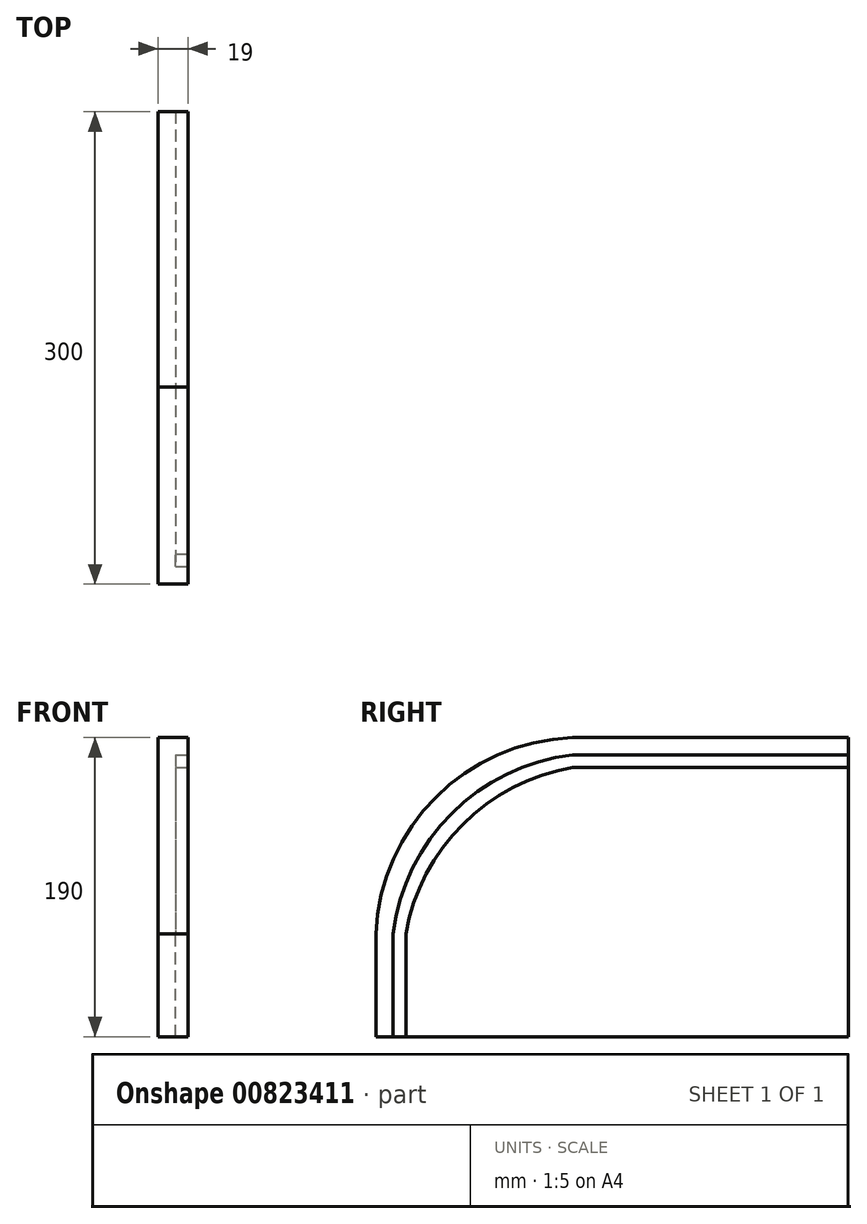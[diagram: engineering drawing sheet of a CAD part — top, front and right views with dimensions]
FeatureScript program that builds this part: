
annotation { "Feature Type Name" : "Feature", "Feature Type Description" : "" }
export const myFeature = defineFeature(function(context is Context, id is Id, definition is map)
    precondition{}
    {
        {
            var Q0;
            Q0=qCreatedBy(makeId("Right.planeOp"),FACE);
            var sketch = newSketch(context, id + "F0", { "sketchPlane" : qUnion([Q0])});
            skLineSegment(sketch, "E0.bottom", {"start": v(-25, 95) * mm, "end": v(150, 95) * mm});
            skLineSegment(sketch, "E0.top", {"start": v(-150, -95) * mm, "end": v(150, -95) * mm});
            skLineSegment(sketch, "E0.left", {"start": v(-150, -29.82) * mm, "end": v(-150, -95) * mm});
            skLineSegment(sketch, "E0.right", {"start": v(150, 95) * mm, "end": v(150, -95) * mm});
            skPoint(sketch, "E0.middle", {"position": v(0, 0) * mm});
            skPoint(sketch, "E1", {"position": v(-150, -40) * mm});
            skPoint(sketch, "E2", {"position": v(-25, 95) * mm});
            skArc(sketch, "E3", {"start": v(-25, 95) * mm, "mid": v(-115.49, 53.42) * mm, "end": v(-150, -40) * mm});
            skPoint(sketch, "E4.orphan", {"position": v(-150, 95) * mm});
            skSolve(sketch);
        }
        {
            var Q0;
            {var subQ5=sQuery(id+"F0.wireOp",EDGE,"E0.bottom");Q0=makeQuery(id+"F0.imprint","IMPRINT",FACE,{"disambiguationData":[TD([[makeQuery(id+"F0.imprint","IMPRINT",EDGE,{"derivedFrom":subQ5}),-1.0]])]});}
            extrude(context, id + "F1", {"entities" : qUnion([Q0]), "depth" : 19 * mm, "offsetDistance" : 25 * mm});
        }
        {
            var Q0;
            Q0=makeQuery(id+"F1.opExtrude","CAP_FACE",FACE,{"disambiguationData":[OSD([sQuery(id+"F0.wireOp",EDGE,"E0.bottom"),sQuery(id+"F0.wireOp",EDGE,"E0.top"),sQuery(id+"F0.wireOp",EDGE,"E0.left"),sQuery(id+"F0.wireOp",EDGE,"E0.right"),sQuery(id+"F0.wireOp",EDGE,"E3")])],"isStart":false});
            var sketch = newSketch(context, id + "F2", { "sketchPlane" : qUnion([Q0])});
            skPoint(sketch, "E5", {"position": v(150, 84) * mm});
            skPoint(sketch, "E6", {"position": v(150, 76) * mm});
            skLineSegment(sketch, "E7", {"start": v(150, 84) * mm, "end": v(-25, 84) * mm});
            skLineSegment(sketch, "E8", {"start": v(150, 76) * mm, "end": v(-25, 76) * mm});
            skPoint(sketch, "E9", {"position": v(-139, -95) * mm});
            skPoint(sketch, "E10", {"position": v(-131, -95) * mm});
            skLineSegment(sketch, "E11", {"start": v(-139, -95) * mm, "end": v(-139, -29.82) * mm});
            skLineSegment(sketch, "E12", {"start": v(-131, -95) * mm, "end": v(-131, -29.82) * mm});
            skArc(sketch, "E13", {"start": v(-25, 76) * mm, "mid": v(-94.77, 39.9) * mm, "end": v(-131, -29.82) * mm});
            skArc(sketch, "E14", {"start": v(-25, 84) * mm, "mid": v(-101.75, 46.88) * mm, "end": v(-139, -29.82) * mm});
            skSolve(sketch);
        }
        {
            var Q0;
            {var subQ1=sQuery(id+"F2.wireOp",EDGE,"E7");Q0=makeQuery(id+"F2.imprint","IMPRINT",FACE,{"disambiguationData":[TD([[makeQuery(id+"F2.imprint","IMPRINT",EDGE,{"derivedFrom":subQ1}),1.0]])]});}
            extrude(context, id + "F3", {"entities" : qUnion([Q0]), "operationType" : NewBodyOperationType.REMOVE, "oppositeDirection" : true, "depth" : 8 * mm, "offsetDistance" : 25 * mm});
        }
    });
